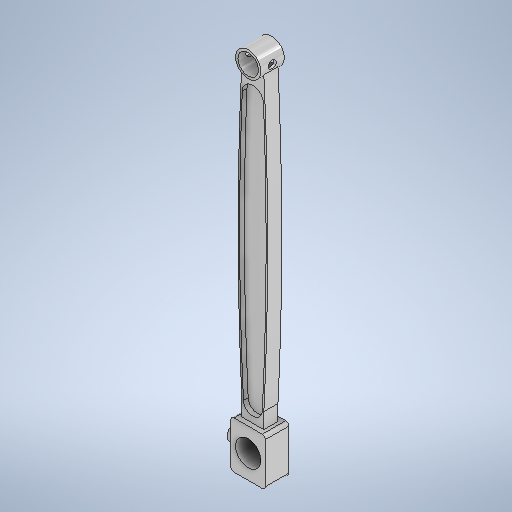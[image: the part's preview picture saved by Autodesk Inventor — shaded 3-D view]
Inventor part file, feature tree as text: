
AUTODESK INVENTOR PART (.ipt)
format: ipt  version: 2025.1 (Build 291241000, 241)  size: 380,416 bytes
history: native  units: mm
features: sketch x9, extrude x6, hole x3, plane x3, projected_geometry x2, fillet x1, mirror x1
ambient origin geometry x8: Origin, YZ Plane, XZ Plane, XY Plane, X Axis, Y Axis, Z Axis, Center Point
bodies: Volumenkörper1 (feature_tree)
feature tree (25):
  extrude  "Extrusion1"  Depth=22.0mm
  extrude  "Extrusion2"  Depth=16.0mm
  fillet  "Rundung1"  Radius=15.0mm
  extrude  "Extrusion3"  Depth=10.0mm
  hole  "Bohrung1"  [1 undecoded]
  plane  "Arbeitsebene1"
  extrude  "Extrusion4"  Depth=16.0mm
  hole  "Bohrung2"  [1 undecoded]
  extrude  "Extrusion5"  Depth=12.0mm
  extrude  "Extrusion6"  Depth=85.0mm
  plane  "Arbeitsebene2"
  mirror  "Spiegeln1"
  plane  "Arbeitsebene3"
  hole  "Bohrung3"  [1 undecoded]
  sketch  "Skizze1"  dims[d0=30.0mm d1=22.0mm]
  sketch  "Skizze2"  dims[d2=15.0mm d3=0.0mm d4=16.0mm d5=15.0mm d6=0.0mm]
  sketch  "Skizze3"  dims[d7=2.0mm d8=10.0mm]
  sketch  "Skizze4"  dims[d9=5.0mm d10=0.0mm]
  sketch  "Skizze5"  dims[d11=4.917mm d12=5.0mm d13=4.0mm d14=2.0mm d15=90.0deg d16=6.0mm d17=0.0mm d18=7.5mm]
  projected_geometry  "Projizierte Kontur1"
  sketch  "Skizze6"  dims[d21=215.0mm d22=16.0mm]
  sketch  "Skizze7"  dims[d23=15.0mm d24=0.0mm]
  projected_geometry  "Projizierte Kontur2"
  sketch  "Skizze8"  dims[d25=13.0mm d26=12.0mm d27=4.0mm d28=2.0mm d29=90.0deg d30=13.0mm d31=0.0mm d35=9.0mm d36=0.0mm]
  sketch  "Skizze9"  dims[d38=25.0mm d40=12.0mm d41=85.0mm d42=3.0mm d43=0.0mm d44=7.5mm d51=14.0mm d52=1800.0mm d53=1800.0mm d55=25.0mm d56=-19.0mm d57=4.917mm d58=3.0mm d59=4.0mm d60=2.0mm d61=90.0deg d62=6.0mm d63=0.0mm d64=14.0mm]
note: 3 required parameter values undecoded (feature->parameter linkage not recoverable at this tier; creation-order binding heuristic only, values carry confidence <= 0.55)
